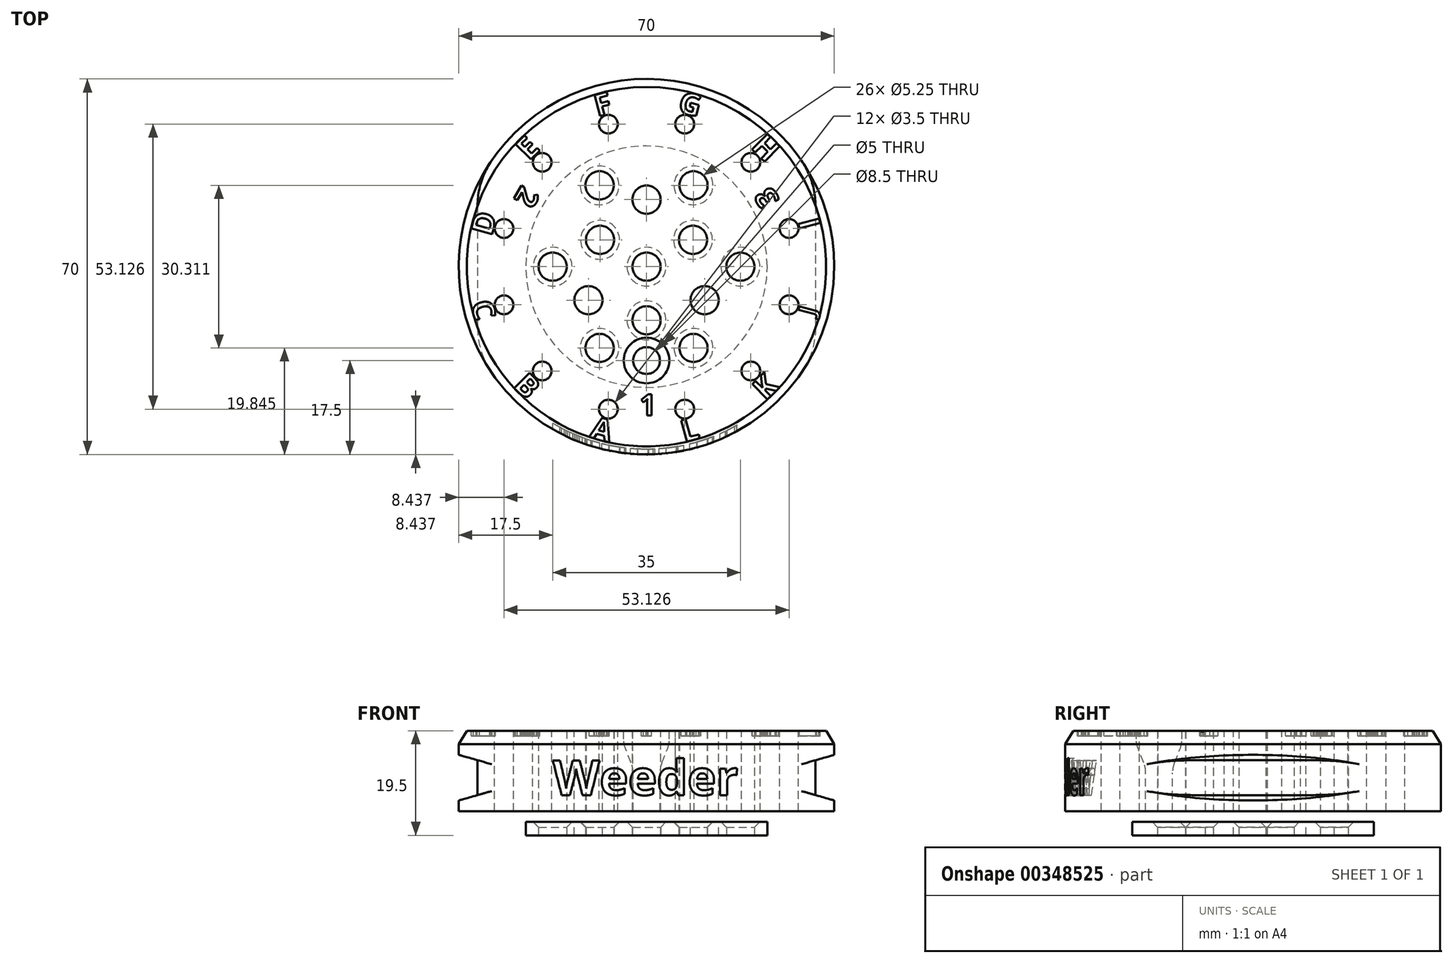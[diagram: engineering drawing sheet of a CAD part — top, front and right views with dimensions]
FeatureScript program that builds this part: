
annotation { "Feature Type Name" : "Feature", "Feature Type Description" : "" }
export const myFeature = defineFeature(function(context is Context, id is Id, definition is map)
    precondition{}
    {
        {
            var Q0;
            Q0=qCreatedBy(makeId("Top.planeOp"),FACE);
            var sketch = newSketch(context, id + "F0", { "sketchPlane" : qUnion([Q0])});
            skCircle(sketch, "E0", {"center": v(0, 0) * mm, "radius": 35 * mm});
            skSolve(sketch);
        }
        {
            var Q0;
            Q0=qSketchRegion(id+"F0",true);
            extrude(context, id + "F1", {"entities" : qUnion([Q0]), "depth" : 15 * mm});
        }
        {
            var Q0;
            Q0=qCreatedBy(makeId("Front.planeOp"),FACE);
            var sketch = newSketch(context, id + "F2", { "sketchPlane" : qUnion([Q0])});
            skText(sketch, "E1", { "text": "Weeder", "fontName": "OpenSans-Bold.ttf"});
            const initialGuessF2  = {"E1": [-0.01747, 0.003, 1, 0, 0.0065]};
            skSetInitialGuess(sketch, initialGuessF2);
            skSolve(sketch);
        }
        {
            var Q0;
            Q0=qSketchRegion(id+"F2",true);
            var Q1;
            Q1=makeQuery(id+"F1.opExtrude","SWEPT_FACE",FACE,{"disambiguationData":[OSD([sQuery(id+"F0.wireOp",EDGE,"E0")])]});
            extrude(context, id + "F3", {"entities" : qUnion([Q0]), "operationType" : NewBodyOperationType.REMOVE, "endBound" : BoundingType.THROUGH_ALL, "endBoundEntityFace" : qUnion([Q1]), "depth" : 25 * mm});
        }
        {
            var Q0;
            Q0=makeQuery(id+"F1.opExtrude","CAP_FACE",FACE,{"disambiguationData":[OSD([sQuery(id+"F0.wireOp",EDGE,"E0")])],"isStart":false});
            var sketch = newSketch(context, id + "F4", { "sketchPlane" : qUnion([Q0])});
            skCircle(sketch, "E2", {"center": v(0, 0) * mm, "radius": 34 * mm});
            skSolve(sketch);
        }
        {
            var Q0;
            Q0=qSketchRegion(id+"F4",true);
            var Q1;
            Q1=makeQuery(id+"F1.opExtrude","CAP_FACE",FACE,{"disambiguationData":[OSD([sQuery(id+"F0.wireOp",EDGE,"E0")])],"isStart":true});
            extrude(context, id + "F5", {"entities" : qUnion([Q0]), "operationType" : NewBodyOperationType.ADD, "endBound" : BoundingType.UP_TO_SURFACE, "oppositeDirection" : true, "endBoundEntityFace" : qUnion([Q1]), "depth" : 25 * mm});
        }
        {
            var Q0;
            Q0=qCreatedBy(makeId("Front.planeOp"),FACE);
            var sketch = newSketch(context, id + "F6", { "sketchPlane" : qUnion([Q0])});
            skLineSegment(sketch, "E3", {"start": v(-35, 10.5) * mm, "end": v(-35, 2) * mm});
            skLineSegment(sketch, "E4", {"start": v(-35, 2) * mm, "end": v(-31.5, 3) * mm});
            skLineSegment(sketch, "E5", {"start": v(-31.5, 3) * mm, "end": v(-31.5, 9.5) * mm});
            skLineSegment(sketch, "E6", {"start": v(-31.5, 9.5) * mm, "end": v(-35, 10.5) * mm});
            skLineSegment(sketch, "E7.MirrorCS", {"start": v(35, 10.5) * mm, "end": v(35, 2) * mm});
            skLineSegment(sketch, "E8.MirrorCS", {"start": v(31.5, 9.5) * mm, "end": v(35, 10.5) * mm});
            skLineSegment(sketch, "E9.MirrorCS", {"start": v(35, 2) * mm, "end": v(31.5, 3) * mm});
            skLineSegment(sketch, "E10.MirrorCS", {"start": v(31.5, 3) * mm, "end": v(31.5, 9.5) * mm});
            skSolve(sketch);
        }
        {
            var Q0;
            Q0=qSketchRegion(id+"F6",true);
            extrude(context, id + "F7", {"entities" : qUnion([Q0]), "operationType" : NewBodyOperationType.REMOVE, "endBound" : BoundingType.THROUGH_ALL, "oppositeDirection" : true, "depth" : 25 * mm, "hasSecondDirection" : true, "secondDirectionBound" : SecondDirectionBoundingType.THROUGH_ALL, "secondDirectionOppositeDirection" : false, "secondDirectionDepth" : 25 * mm});
        }
        {
            var Q0;
            {var subQ0=sQuery(id+"F0.wireOp",EDGE,"E0");Q0=makeQuery(id+"F7.boolean.opBoolean","INTERSECT",EDGE,{"disambiguationData":[OD(0.0)],"derivedFrom":[makeQuery(id+"F3.boolean.opBoolean","SPLIT",FACE,{"disambiguationData":[TD([makeQuery(id+"F1.opExtrude","CAP_FACE",FACE,{"disambiguationData":[OSD([subQ0])],"isStart":true})])],"derivedFrom":makeQuery(id+"F1.opExtrude","SWEPT_FACE",FACE,{"disambiguationData":[OSD([subQ0])]})}),makeQuery(id+"F7.opExtrude","SWEPT_FACE",FACE,{"disambiguationData":[OSD([sQuery(id+"F6.wireOp",EDGE,"E5")])]})]});}
            var Q1;
            {var subQ0=sQuery(id+"F0.wireOp",EDGE,"E0");Q1=makeQuery(id+"F7.boolean.opBoolean","INTERSECT",EDGE,{"disambiguationData":[OD(0.0)],"derivedFrom":[makeQuery(id+"F3.boolean.opBoolean","SPLIT",FACE,{"disambiguationData":[TD([makeQuery(id+"F1.opExtrude","CAP_FACE",FACE,{"disambiguationData":[OSD([subQ0])],"isStart":true})])],"derivedFrom":makeQuery(id+"F1.opExtrude","SWEPT_FACE",FACE,{"disambiguationData":[OSD([subQ0])]})}),makeQuery(id+"F7.opExtrude","SWEPT_FACE",FACE,{"disambiguationData":[OSD([sQuery(id+"F6.wireOp",EDGE,"E10.MirrorCS")])]})]});}
            var Q2;
            {var subQ0=sQuery(id+"F0.wireOp",EDGE,"E0");Q2=makeQuery(id+"F7.boolean.opBoolean","INTERSECT",EDGE,{"disambiguationData":[OD(1.0)],"derivedFrom":[makeQuery(id+"F3.boolean.opBoolean","SPLIT",FACE,{"disambiguationData":[TD([makeQuery(id+"F1.opExtrude","CAP_FACE",FACE,{"disambiguationData":[OSD([subQ0])],"isStart":true})])],"derivedFrom":makeQuery(id+"F1.opExtrude","SWEPT_FACE",FACE,{"disambiguationData":[OSD([subQ0])]})}),makeQuery(id+"F7.opExtrude","SWEPT_FACE",FACE,{"disambiguationData":[OSD([sQuery(id+"F6.wireOp",EDGE,"E10.MirrorCS")])]})]});}
            var Q3;
            {var subQ0=sQuery(id+"F0.wireOp",EDGE,"E0");Q3=makeQuery(id+"F7.boolean.opBoolean","INTERSECT",EDGE,{"disambiguationData":[OD(1.0)],"derivedFrom":[makeQuery(id+"F3.boolean.opBoolean","SPLIT",FACE,{"disambiguationData":[TD([makeQuery(id+"F1.opExtrude","CAP_FACE",FACE,{"disambiguationData":[OSD([subQ0])],"isStart":true})])],"derivedFrom":makeQuery(id+"F1.opExtrude","SWEPT_FACE",FACE,{"disambiguationData":[OSD([subQ0])]})}),makeQuery(id+"F7.opExtrude","SWEPT_FACE",FACE,{"disambiguationData":[OSD([sQuery(id+"F6.wireOp",EDGE,"E5")])]})]});}
            fillet(context, id + "F8", {"entities" : qUnion([Q0, Q1, Q2, Q3]), "radius" : 15 * mm, "tangentPropagation" : true, "allowEdgeOverflow" : false});
        }
        {
            var Q0;
            Q0=makeQuery(id+"F1.opExtrude","CAP_FACE",FACE,{"disambiguationData":[OSD([sQuery(id+"F0.wireOp",EDGE,"E0")])],"isStart":false});
            var sketch = newSketch(context, id + "F9", { "sketchPlane" : qUnion([Q0])});
            skCircle(sketch, "E11", {"center": v(0, 12.5) * mm, "radius": 2.62 * mm});
            skCircle(sketch, "E12.1.0", {"center": v(-10.83, -6.25) * mm, "radius": 2.62 * mm});
            skCircle(sketch, "E12.2.0", {"center": v(10.83, -6.25) * mm, "radius": 2.62 * mm});
            skPoint(sketch, "E12.center", {"position": v(0, 0) * mm});
            skCircle(sketch, "E13", {"center": v(0, 0) * mm, "radius": 12.5 * mm, "construction": true});
            skSolve(sketch);
        }
        {
            var Q0;
            Q0=qSketchRegion(id+"F9",true);
            extrude(context, id + "F10", {"entities" : qUnion([Q0]), "operationType" : NewBodyOperationType.REMOVE, "endBound" : BoundingType.THROUGH_ALL, "oppositeDirection" : true, "depth" : 25 * mm});
        }
        {
            var Q0;
            Q0=makeQuery(id+"F1.opExtrude","CAP_FACE",FACE,{"disambiguationData":[OSD([sQuery(id+"F0.wireOp",EDGE,"E0")])],"isStart":false});
            var sketch = newSketch(context, id + "F11", { "sketchPlane" : qUnion([Q0])});
            skCircle(sketch, "E14", {"center": v(0, -17.5) * mm, "radius": 2.5 * mm});
            skCircle(sketch, "E15", {"center": v(0, 0) * mm, "radius": 17.5 * mm, "construction": true});
            skSolve(sketch);
        }
        {
            var Q0;
            Q0=qSketchRegion(id+"F11",true);
            extrude(context, id + "F12", {"entities" : qUnion([Q0]), "operationType" : NewBodyOperationType.REMOVE, "endBound" : BoundingType.THROUGH_ALL, "oppositeDirection" : true, "depth" : 25 * mm});
        }
        {
            var Q0;
            Q0=makeQuery(id+"F1.opExtrude","CAP_FACE",FACE,{"disambiguationData":[OSD([sQuery(id+"F0.wireOp",EDGE,"E0")])],"isStart":false});
            var sketch = newSketch(context, id + "F13", { "sketchPlane" : qUnion([Q0])});
            skCircle(sketch, "E16", {"center": v(0, -17.5) * mm, "radius": 4.25 * mm});
            skSolve(sketch);
        }
        {
            var Q0;
            Q0=qSketchRegion(id+"F13",true);
            extrude(context, id + "F14", {"entities" : qUnion([Q0]), "operationType" : NewBodyOperationType.REMOVE, "oppositeDirection" : true, "depth" : 7.5 * mm});
        }
        {
            var Q0;
            Q0=makeQuery(id+"F14.boolean.opBoolean","COPY",EDGE,{"derivedFrom":makeQuery(id+"F14.opExtrude","CAP_EDGE",EDGE,{"disambiguationData":[OSD([sQuery(id+"F13.wireOp",EDGE,"E16")])],"isStart":false})});
            chamfer(context, id + "F15", {"entities" : qUnion([Q0]), "chamferType" : ChamferType.TWO_OFFSETS, "width1" : 5 * mm, "oppositeDirection" : true, "width2" : 2 * mm, "tangentPropagation" : true});
        }
        {
            var Q0;
            {var subQ0=sQuery(id+"F13.wireOp",EDGE,"E16");Q0=makeQuery(id+"F15.opChamfer","BLEND_EDGE",EDGE,{"blendedFrom":[makeQuery(id+"F14.boolean.opBoolean","COPY",EDGE,{"derivedFrom":makeQuery(id+"F14.opExtrude","CAP_EDGE",EDGE,{"disambiguationData":[OSD([subQ0])],"isStart":false})}),makeQuery(id+"F14.boolean.opBoolean","COPY",FACE,{"derivedFrom":makeQuery(id+"F14.opExtrude","SWEPT_FACE",FACE,{"disambiguationData":[OSD([subQ0])]})})],"blendedInto":[makeQuery(id+"F14.boolean.opBoolean","COPY",FACE,{"derivedFrom":makeQuery(id+"F14.opExtrude","SWEPT_FACE",FACE,{"disambiguationData":[OSD([subQ0])]})})]});}
            var Q1;
            Q1=makeQuery(id+"F15.opChamfer","BLEND_EDGE",EDGE,{"blendedFrom":[makeQuery(id+"F14.boolean.opBoolean","COPY",EDGE,{"derivedFrom":makeQuery(id+"F14.opExtrude","CAP_EDGE",EDGE,{"disambiguationData":[OSD([sQuery(id+"F13.wireOp",EDGE,"E16")])],"isStart":false})}),makeQuery(id+"F12.boolean.opBoolean","COPY",FACE,{"derivedFrom":makeQuery(id+"F12.opExtrude","SWEPT_FACE",FACE,{"disambiguationData":[OSD([sQuery(id+"F11.wireOp",EDGE,"E14")])]})})],"blendedInto":[makeQuery(id+"F12.boolean.opBoolean","COPY",FACE,{"derivedFrom":makeQuery(id+"F12.opExtrude","SWEPT_FACE",FACE,{"disambiguationData":[OSD([sQuery(id+"F11.wireOp",EDGE,"E14")])]})})]});
            fillet(context, id + "F16", {"entities" : qUnion([Q0, Q1]), "radius" : 5 * mm, "tangentPropagation" : true, "allowEdgeOverflow" : false});
        }
        {
            var Q0;
            Q0=makeQuery(id+"F1.opExtrude","CAP_FACE",FACE,{"disambiguationData":[OSD([sQuery(id+"F0.wireOp",EDGE,"E0")])],"isStart":false});
            var sketch = newSketch(context, id + "F17", { "sketchPlane" : qUnion([Q0])});
            skCircle(sketch, "E17", {"center": v(19.45, 19.45) * mm, "radius": 1.75 * mm});
            skCircle(sketch, "E18", {"center": v(0, 0) * mm, "radius": 27.5 * mm, "construction": true});
            skLineSegment(sketch, "E19", {"start": v(0, 0) * mm, "end": v(19.45, 19.45) * mm, "construction": true});
            skCircle(sketch, "E20.1.1", {"center": v(7.12, 26.56) * mm, "radius": 1.75 * mm});
            skCircle(sketch, "E20.2.1", {"center": v(-7.12, 26.56) * mm, "radius": 1.75 * mm});
            skCircle(sketch, "E20.3.1", {"center": v(-19.45, 19.45) * mm, "radius": 1.75 * mm});
            skCircle(sketch, "E20.4.1", {"center": v(-26.56, 7.12) * mm, "radius": 1.75 * mm});
            skCircle(sketch, "E20.5.1", {"center": v(-26.56, -7.12) * mm, "radius": 1.75 * mm});
            skCircle(sketch, "E20.6.1", {"center": v(-19.45, -19.45) * mm, "radius": 1.75 * mm});
            skCircle(sketch, "E20.7.1", {"center": v(-7.12, -26.56) * mm, "radius": 1.75 * mm});
            skCircle(sketch, "E20.8.1", {"center": v(7.12, -26.56) * mm, "radius": 1.75 * mm});
            skCircle(sketch, "E20.9.1", {"center": v(19.45, -19.45) * mm, "radius": 1.75 * mm});
            skCircle(sketch, "E20.10.1", {"center": v(26.56, -7.12) * mm, "radius": 1.75 * mm});
            skCircle(sketch, "E20.11.1", {"center": v(26.56, 7.12) * mm, "radius": 1.75 * mm});
            skSolve(sketch);
        }
        {
            var Q0;
            Q0=qSketchRegion(id+"F17",true);
            extrude(context, id + "F18", {"entities" : qUnion([Q0]), "operationType" : NewBodyOperationType.REMOVE, "endBound" : BoundingType.THROUGH_ALL, "oppositeDirection" : true, "depth" : 25 * mm});
        }
        {
            var Q0;
            Q0=makeQuery(id+"F1.opExtrude","CAP_EDGE",EDGE,{"disambiguationData":[OSD([sQuery(id+"F0.wireOp",EDGE,"E0")])],"isStart":false});
            chamfer(context, id + "F19", {"entities" : qUnion([Q0]), "chamferType" : ChamferType.TWO_OFFSETS, "width1" : 2.5 * mm, "oppositeDirection" : true, "width2" : 1.5 * mm, "tangentPropagation" : true});
        }
        {
            var Q0;
            Q0=makeQuery(id+"F1.opExtrude","CAP_FACE",FACE,{"disambiguationData":[OSD([sQuery(id+"F0.wireOp",EDGE,"E0")])],"isStart":false});
            var sketch = newSketch(context, id + "F20", { "sketchPlane" : qUnion([Q0])});
            skText(sketch, "E21", { "text": "A", "fontName": "OpenSans-Bold.ttf"});
            skText(sketch, "E22", { "text": "B", "fontName": "OpenSans-Bold.ttf"});
            skText(sketch, "E23", { "text": "C", "fontName": "OpenSans-Bold.ttf"});
            skText(sketch, "E24", { "text": "E", "fontName": "OpenSans-Bold.ttf"});
            skText(sketch, "E25", { "text": "F", "fontName": "OpenSans-Bold.ttf"});
            skText(sketch, "E26", { "text": "G", "fontName": "OpenSans-Bold.ttf"});
            skText(sketch, "E27", { "text": "H", "fontName": "OpenSans-Bold.ttf"});
            skText(sketch, "E28", { "text": "I", "fontName": "OpenSans-Bold.ttf"});
            skText(sketch, "E29", { "text": "J", "fontName": "OpenSans-Bold.ttf"});
            skText(sketch, "E30", { "text": "K", "fontName": "OpenSans-Bold.ttf"});
            skText(sketch, "E31", { "text": "L", "fontName": "OpenSans-Bold.ttf"});
            skText(sketch, "E32", { "text": "D", "fontName": "OpenSans-Bold.ttf"});
            skCircle(sketch, "E33", {"center": v(0, 0) * mm, "radius": 29.38 * mm, "construction": true});
            skText(sketch, "E34", { "text": "1", "fontName": "OpenSans-Bold.ttf"});
            skText(sketch, "E35", { "text": "2", "fontName": "OpenSans-Bold.ttf"});
            skText(sketch, "E36", { "text": "3", "fontName": "OpenSans-Bold.ttf"});
            skCircle(sketch, "E37", {"center": v(0, 0) * mm, "radius": 23.75 * mm, "construction": true});
            const initialGuessF20  = {"E21": [-0.0107, -0.03174, 0.96593, -0.25882, 0.00406], "E22": [-0.025, -0.02228, 0.7071, -0.7071, 0.00406], "E23": [-0.03278, -0.00684, 0.25882, -0.96593, 0.00406], "E24": [-0.0219, 0.01964, 0.7071, 0.7071, 0.00406], "E25": [-0.00914, 0.02796, 0.96593, 0.25882, 0.00406], "E26": [0.00567, 0.0289, 0.96593, -0.25882, 0.00406], "E27": [0.0193, 0.02225, 0.7071, -0.7071, 0.00406], "E28": [0.02815, 0.00844, 0.25882, -0.96593, 0.00406], "E29": [0.0313, -0.00927, 0.25882, 0.96593, 0.00325], "E30": [0.02219, -0.0251, 0.7071, 0.7071, 0.00406], "E31": [0.00703, -0.03273, 0.96593, 0.25882, 0.00406], "E32": [-0.02892, 0.00557, 0.25882, 0.96593, 0.00406], "E34": [-0.00133, -0.02775, 1, 0, 0.004], "E35": [-0.0232, 0.01533, -0.5, -0.86603, 0.004], "E36": [0.02486, 0.01244, -0.5, 0.86603, 0.004]};
            skSetInitialGuess(sketch, initialGuessF20);
            skSolve(sketch);
        }
        {
            var Q0;
            Q0=qSketchRegion(id+"F20",true);
            extrude(context, id + "F21", {"entities" : qUnion([Q0]), "operationType" : NewBodyOperationType.REMOVE, "oppositeDirection" : true, "depth" : 1 * mm});
        }
        {
            var Q0;
            Q0=makeQuery(id+"F1.opExtrude","CAP_FACE",FACE,{"disambiguationData":[OSD([sQuery(id+"F0.wireOp",EDGE,"E0")])],"isStart":true});
            cPlane(context, id + "F22", {"entities" : qUnion([Q0]), "cplaneType" : CPlaneType.OFFSET, "offset" : 2 * mm, "width" : 150 * mm, "height" : 150 * mm});
        }
        {
            var Q0;
            Q0=qCreatedBy(id+"F22.planeOp",FACE);
            var sketch = newSketch(context, id + "F23", { "sketchPlane" : qUnion([Q0])});
            skCircle(sketch, "E38.0", {"center": v(-10.83, 6.25) * mm, "radius": 2.62 * mm});
            skCircle(sketch, "E38.1", {"center": v(10.83, 6.25) * mm, "radius": 2.62 * mm});
            skCircle(sketch, "E38.2", {"center": v(0, -12.5) * mm, "radius": 2.62 * mm});
            skCircle(sketch, "E39", {"center": v(0, 0) * mm, "radius": 22.5 * mm});
            skSolve(sketch);
        }
        {
            var Q0;
            Q0=qSketchRegion(id+"F23",true);
            extrude(context, id + "F24", {"entities" : qUnion([Q0]), "depth" : 2.5 * mm});
        }
        {
            var Q0;
            Q0=makeQuery(id+"F24.opExtrude","CAP_FACE",FACE,{"disambiguationData":[OSD([sQuery(id+"F23.wireOp",EDGE,"E38.0"),sQuery(id+"F23.wireOp",EDGE,"E38.1"),sQuery(id+"F23.wireOp",EDGE,"E38.2"),sQuery(id+"F23.wireOp",EDGE,"E39")])],"isStart":false});
            var sketch = newSketch(context, id + "F25", { "sketchPlane" : qUnion([Q0])});
            skCircle(sketch, "E40", {"center": v(0, 0) * mm, "radius": 2.62 * mm});
            skCircle(sketch, "E41", {"center": v(0, 10) * mm, "radius": 2.62 * mm});
            skCircle(sketch, "E42.1.0", {"center": v(-8.66, -5) * mm, "radius": 2.62 * mm});
            skCircle(sketch, "E42.2.0", {"center": v(8.66, -5) * mm, "radius": 2.62 * mm});
            skCircle(sketch, "E43", {"center": v(-8.75, 15.16) * mm, "radius": 2.62 * mm});
            skLineSegment(sketch, "E44", {"start": v(-8.75, 15.16) * mm, "end": v(0, 0) * mm, "construction": true});
            skLineSegment(sketch, "E45", {"start": v(0, 0) * mm, "end": v(0, 10) * mm, "construction": true});
            skCircle(sketch, "E46.1.0", {"center": v(-17.5, 0) * mm, "radius": 2.62 * mm});
            skCircle(sketch, "E46.2.0", {"center": v(-8.75, -15.16) * mm, "radius": 2.62 * mm});
            skCircle(sketch, "E46.3.0", {"center": v(8.75, -15.16) * mm, "radius": 2.62 * mm});
            skCircle(sketch, "E46.4.0", {"center": v(17.5, 0) * mm, "radius": 2.62 * mm});
            skCircle(sketch, "E46.5.0", {"center": v(8.75, 15.16) * mm, "radius": 2.62 * mm});
            skSolve(sketch);
        }
        {
            var Q0;
            Q0=qSketchRegion(id+"F25",true);
            extrude(context, id + "F26", {"entities" : qUnion([Q0]), "operationType" : NewBodyOperationType.REMOVE, "endBound" : BoundingType.THROUGH_ALL, "oppositeDirection" : true, "depth" : 25 * mm});
        }
        {
            var Q0;
            Q0=makeQuery(id+"F26.boolean.opBoolean","INTERSECT",EDGE,{"derivedFrom":[makeQuery(id+"F24.opExtrude","CAP_FACE",FACE,{"disambiguationData":[OSD([sQuery(id+"F23.wireOp",EDGE,"E38.0"),sQuery(id+"F23.wireOp",EDGE,"E38.1"),sQuery(id+"F23.wireOp",EDGE,"E38.2"),sQuery(id+"F23.wireOp",EDGE,"E39")])],"isStart":true}),makeQuery(id+"F26.opExtrude","SWEPT_FACE",FACE,{"disambiguationData":[OSD([sQuery(id+"F25.wireOp",EDGE,"E40")])]})]});
            var Q1;
            Q1=makeQuery(id+"F26.boolean.opBoolean","INTERSECT",EDGE,{"derivedFrom":[makeQuery(id+"F24.opExtrude","CAP_FACE",FACE,{"disambiguationData":[OSD([sQuery(id+"F23.wireOp",EDGE,"E38.0"),sQuery(id+"F23.wireOp",EDGE,"E38.1"),sQuery(id+"F23.wireOp",EDGE,"E38.2"),sQuery(id+"F23.wireOp",EDGE,"E39")])],"isStart":true}),makeQuery(id+"F26.opExtrude","SWEPT_FACE",FACE,{"disambiguationData":[OSD([sQuery(id+"F25.wireOp",EDGE,"E41")])]})]});
            var Q2;
            Q2=makeQuery(id+"F26.boolean.opBoolean","INTERSECT",EDGE,{"derivedFrom":[makeQuery(id+"F24.opExtrude","CAP_FACE",FACE,{"disambiguationData":[OSD([sQuery(id+"F23.wireOp",EDGE,"E38.0"),sQuery(id+"F23.wireOp",EDGE,"E38.1"),sQuery(id+"F23.wireOp",EDGE,"E38.2"),sQuery(id+"F23.wireOp",EDGE,"E39")])],"isStart":true}),makeQuery(id+"F26.opExtrude","SWEPT_FACE",FACE,{"disambiguationData":[OSD([sQuery(id+"F25.wireOp",EDGE,"E46.2.0")])]})]});
            var Q3;
            Q3=makeQuery(id+"F26.boolean.opBoolean","INTERSECT",EDGE,{"derivedFrom":[makeQuery(id+"F24.opExtrude","CAP_FACE",FACE,{"disambiguationData":[OSD([sQuery(id+"F23.wireOp",EDGE,"E38.0"),sQuery(id+"F23.wireOp",EDGE,"E38.1"),sQuery(id+"F23.wireOp",EDGE,"E38.2"),sQuery(id+"F23.wireOp",EDGE,"E39")])],"isStart":true}),makeQuery(id+"F26.opExtrude","SWEPT_FACE",FACE,{"disambiguationData":[OSD([sQuery(id+"F25.wireOp",EDGE,"E46.1.0")])]})]});
            var Q4;
            Q4=makeQuery(id+"F26.boolean.opBoolean","INTERSECT",EDGE,{"derivedFrom":[makeQuery(id+"F24.opExtrude","CAP_FACE",FACE,{"disambiguationData":[OSD([sQuery(id+"F23.wireOp",EDGE,"E38.0"),sQuery(id+"F23.wireOp",EDGE,"E38.1"),sQuery(id+"F23.wireOp",EDGE,"E38.2"),sQuery(id+"F23.wireOp",EDGE,"E39")])],"isStart":true}),makeQuery(id+"F26.opExtrude","SWEPT_FACE",FACE,{"disambiguationData":[OSD([sQuery(id+"F25.wireOp",EDGE,"E43")])]})]});
            var Q5;
            Q5=makeQuery(id+"F26.boolean.opBoolean","INTERSECT",EDGE,{"derivedFrom":[makeQuery(id+"F24.opExtrude","CAP_FACE",FACE,{"disambiguationData":[OSD([sQuery(id+"F23.wireOp",EDGE,"E38.0"),sQuery(id+"F23.wireOp",EDGE,"E38.1"),sQuery(id+"F23.wireOp",EDGE,"E38.2"),sQuery(id+"F23.wireOp",EDGE,"E39")])],"isStart":true}),makeQuery(id+"F26.opExtrude","SWEPT_FACE",FACE,{"disambiguationData":[OSD([sQuery(id+"F25.wireOp",EDGE,"E46.5.0")])]})]});
            var Q6;
            Q6=makeQuery(id+"F26.boolean.opBoolean","INTERSECT",EDGE,{"derivedFrom":[makeQuery(id+"F24.opExtrude","CAP_FACE",FACE,{"disambiguationData":[OSD([sQuery(id+"F23.wireOp",EDGE,"E38.0"),sQuery(id+"F23.wireOp",EDGE,"E38.1"),sQuery(id+"F23.wireOp",EDGE,"E38.2"),sQuery(id+"F23.wireOp",EDGE,"E39")])],"isStart":true}),makeQuery(id+"F26.opExtrude","SWEPT_FACE",FACE,{"disambiguationData":[OSD([sQuery(id+"F25.wireOp",EDGE,"E46.4.0")])]})]});
            var Q7;
            Q7=makeQuery(id+"F26.boolean.opBoolean","INTERSECT",EDGE,{"derivedFrom":[makeQuery(id+"F24.opExtrude","CAP_FACE",FACE,{"disambiguationData":[OSD([sQuery(id+"F23.wireOp",EDGE,"E38.0"),sQuery(id+"F23.wireOp",EDGE,"E38.1"),sQuery(id+"F23.wireOp",EDGE,"E38.2"),sQuery(id+"F23.wireOp",EDGE,"E39")])],"isStart":true}),makeQuery(id+"F26.opExtrude","SWEPT_FACE",FACE,{"disambiguationData":[OSD([sQuery(id+"F25.wireOp",EDGE,"E46.3.0")])]})]});
            var Q8;
            Q8=makeQuery(id+"F26.boolean.opBoolean","INTERSECT",EDGE,{"derivedFrom":[makeQuery(id+"F24.opExtrude","CAP_FACE",FACE,{"disambiguationData":[OSD([sQuery(id+"F23.wireOp",EDGE,"E38.0"),sQuery(id+"F23.wireOp",EDGE,"E38.1"),sQuery(id+"F23.wireOp",EDGE,"E38.2"),sQuery(id+"F23.wireOp",EDGE,"E39")])],"isStart":true}),makeQuery(id+"F26.opExtrude","SWEPT_FACE",FACE,{"disambiguationData":[OSD([sQuery(id+"F25.wireOp",EDGE,"E42.1.0")])]})]});
            var Q9;
            Q9=makeQuery(id+"F26.boolean.opBoolean","INTERSECT",EDGE,{"derivedFrom":[makeQuery(id+"F24.opExtrude","CAP_FACE",FACE,{"disambiguationData":[OSD([sQuery(id+"F23.wireOp",EDGE,"E38.0"),sQuery(id+"F23.wireOp",EDGE,"E38.1"),sQuery(id+"F23.wireOp",EDGE,"E38.2"),sQuery(id+"F23.wireOp",EDGE,"E39")])],"isStart":true}),makeQuery(id+"F26.opExtrude","SWEPT_FACE",FACE,{"disambiguationData":[OSD([sQuery(id+"F25.wireOp",EDGE,"E42.2.0")])]})]});
            chamfer(context, id + "F27", {"entities" : qUnion([Q0, Q1, Q2, Q3, Q4, Q5, Q6, Q7, Q8, Q9]), "width" : 1 * mm, "tangentPropagation" : true});
        }
    });
